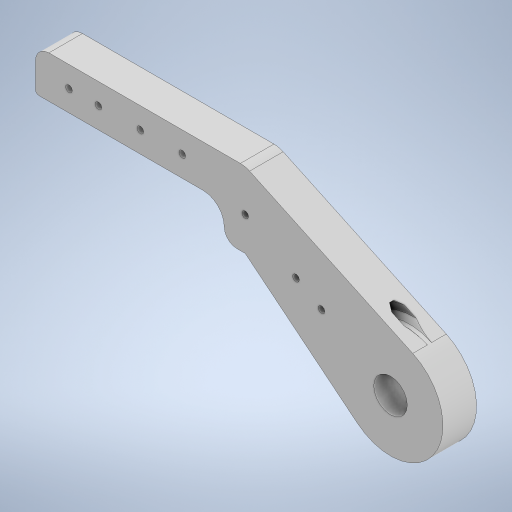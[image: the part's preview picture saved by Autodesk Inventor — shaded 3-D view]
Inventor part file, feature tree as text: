
AUTODESK INVENTOR PART (.ipt)
format: ipt  version: 2024.2 (Build 282272000, 272)  size: 353,792 bytes
history: native  units: mm
features: fillet x3, extrude x2, other x1, sketch x1, chamfer x1
ambient origin geometry x8: Origin, YZ Plane, XZ Plane, XY Plane, X Axis, Y Axis, Z Axis, Center Point
bodies: Body1 (feature_tree)
feature tree (8):
  other  "Bryła1"
  sketch  "Szkic1"
  extrude  "Wyciągnięcie proste1"  Depth=25.0mm
  extrude  "Wyciągnięcie proste2"  Depth=32.0mm
  fillet  "Zaokrąglenie2"  Radius=8.0mm
  fillet  "Zaokrąglenie3"  Radius=40.0mm
  chamfer  "Faza1"  Angle=30.0deg  [1 undecoded]
  fillet  "Zaokrąglenie4"  Radius=50.0mm
note: 1 required parameter value undecoded (feature->parameter linkage not recoverable at this tier; creation-order binding heuristic only, values carry confidence <= 0.55)
